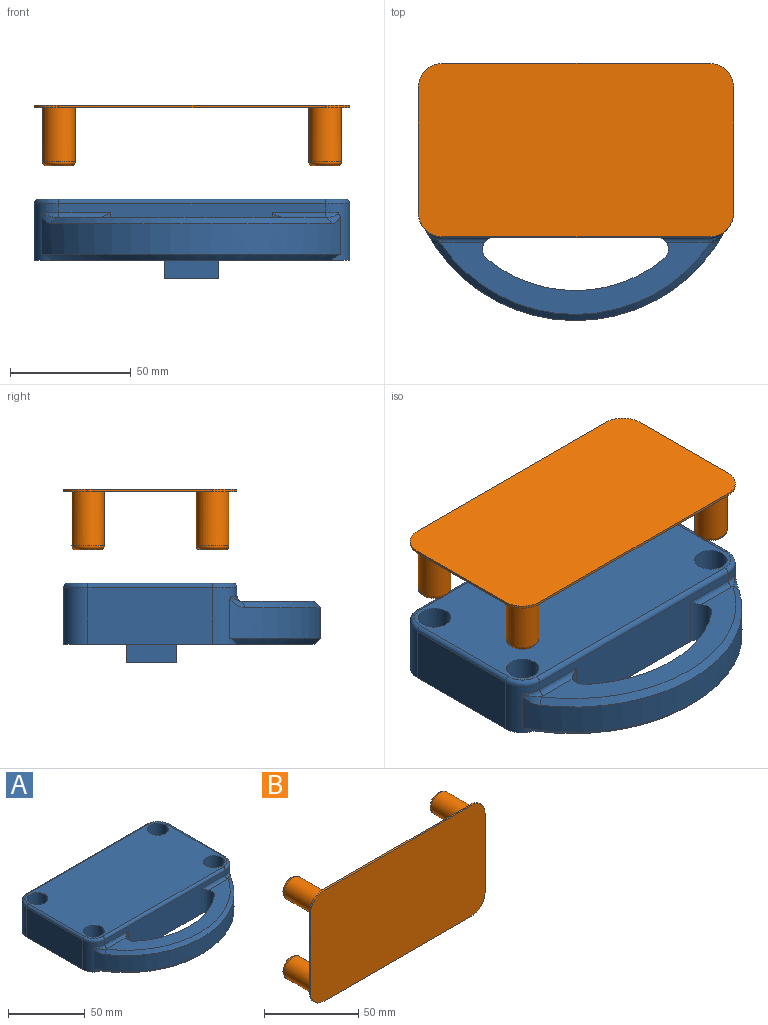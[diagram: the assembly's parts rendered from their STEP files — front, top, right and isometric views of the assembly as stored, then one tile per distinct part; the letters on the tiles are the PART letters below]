
ASSEMBLY  parts=2 mates=1
PART A: 40 faces, bbox 132.5x107.4x33 mm
  f0: plane 130.81x104.06mm, normal (0,0,-1), area 9557.4mm2, adj f1,f2,f3,f4,f5,f6,f7,f8
  f1: cylinder r=10.16mm len=23.5mm, axis (0,0,-1), area 222.8mm2, adj f0,f5,f6,f20,f23,f27,f33,f34
  f2: cylinder r=10.16mm len=23.5mm, axis (0,0,-1), area 375mm2, adj f0,f3,f12,f15
  f3: plane 110.49x23.5mm, normal (0,1,0), area 2596mm2, adj f0,f2,f4,f14
  f4: cylinder r=10.16mm len=23.5mm, axis (0,0,-1), area 375mm2, adj f0,f3,f5,f16
  f5: plane 51.64x23.5mm, normal (-1,0,0), area 1213.3mm2, adj f0,f1,f4,f18
  f6: plane 110.49x23.5mm, normal (0,-1,0), area 1729.2mm2, adj f0,f1,f7,f21,f25,f28,f29,f30
  f7: cylinder r=10.16mm len=23.5mm, axis (0,0,-1), area 247.5mm2, adj f0,f6,f12,f19,f23,f26,f31,f34
  f8: cylinder r=6.75mm len=25.4mm, axis (0,0,-1), area 1077.5mm2, adj f0,f13
  f9: cylinder r=6.75mm len=25.4mm, axis (0,0,-1), area 1077.5mm2, adj f0,f13
  f10: cylinder r=6.75mm len=25.4mm, axis (0,0,-1), area 1077.5mm2, adj f0,f13
  f11: cylinder r=6.75mm len=25.4mm, axis (0,0,-1), area 1077.5mm2, adj f0,f13
  f12: plane 51.64x23.5mm, normal (1,0,0), area 1213.3mm2, adj f0,f2,f7,f17
  f13: plane 127x68.15mm, normal (0,0,1), area 8023.7mm2, adj f8,f9,f10,f11,f14,f15,f16,f17
  f14: cylinder r=1.91mm len=110.49mm, axis (1,0,0), area 330.6mm2, adj f3,f13,f15,f16
  f15: torus R=8.26mm, axis (0,0,1), area 44.5mm2, adj f2,f13,f14,f17
  f16: torus R=8.26mm, axis (0,0,1), area 44.5mm2, adj f4,f13,f14,f18
  f17: cylinder r=1.91mm len=51.64mm, axis (0,-1,0), area 154.5mm2, adj f12,f13,f15,f19
  f18: cylinder r=1.91mm len=51.64mm, axis (0,1,0), area 154.5mm2, adj f5,f13,f16,f20
  f19: torus R=8.26mm, axis (0,0,1), area 44.5mm2, adj f7,f13,f17,f21
  f20: torus R=8.26mm, axis (0,0,1), area 44.5mm2, adj f1,f13,f18,f21
  f21: cylinder r=1.91mm len=110.49mm, axis (-1,0,0), area 330.6mm2, adj f6,f13,f19,f20
  f22: cylinder r=57.75mm len=73.49mm, axis (0,0,-1), area 1416.1mm2, adj f0,f24,f29,f30
  f23: cylinder r=70.2mm len=123.92mm, axis (0,0,-1), area 1951.8mm2, adj f1,f7,f31,f32,f33,f34
  f24: plane 112.4x30mm, normal (0,0,1), area 1180.6mm2, adj f22,f25,f26,f27,f28,f29,f30,f32
  f25: cylinder r=2.16mm len=21.98mm, axis (-1,0,0), area 67.5mm2, adj f6,f24,f26,f30
  f26: torus R=12.32mm, axis (0,0,-1), area 12.5mm2, adj f7,f24,f25,f31
  f27: torus R=12.32mm, axis (0,0,-1), area 15.1mm2, adj f1,f24,f28,f33
  f28: cylinder r=2.16mm len=21.49mm, axis (-1,0,0), area 65.8mm2, adj f6,f24,f27,f29
  f29: cylinder r=5.08mm len=19.94mm, axis (0,0,-1), area 226.7mm2, adj f0,f6,f22,f24,f28
  f30: cylinder r=5.08mm len=19.94mm, axis (0,0,-1), area 226.7mm2, adj f0,f6,f22,f24,f25
  f31: bspline ~6.22x5.83mm, area 18.5mm2, adj f7,f23,f26,f32
  f32: cone r=67.66mm half-angle=45deg, axis (0,0,-1), area 485.4mm2, adj f23,f24,f31,f33
  f33: bspline ~6.92x6.19mm, area 19.6mm2, adj f1,f23,f27,f32
  f34: cone r=70.2mm half-angle=45deg, axis (0,0,1), area 521.1mm2, adj f0,f1,f7,f23
  f35: plane 20.53x7.62mm, normal (-1,0,0), area 156.5mm2, adj f0,f36,f38,f39
  f36: plane 22.57x7.62mm, normal (0,1,0), area 172mm2, adj f0,f35,f37,f39
  f37: plane 20.53x7.62mm, normal (1,0,0), area 156.5mm2, adj f0,f36,f38,f39
  f38: plane 22.57x7.62mm, normal (0,-1,0), area 172mm2, adj f0,f35,f37,f39
  f39: plane 22.57x20.53mm, normal (0,0,-1), area 463.4mm2, adj f35,f36,f37,f38
PART B: 22 faces, bbox 130.8x25x72 mm
  f0: cylinder r=10.16mm len=10.16mm, axis (0,-1,0), area 16mm2, adj f1,f7,f8,f9
  f1: plane 110.49x1mm, normal (0,0,1), area 110.5mm2, adj f0,f2,f8,f9
  f2: cylinder r=10.16mm len=10.16mm, axis (0,-1,0), area 16mm2, adj f1,f3,f8,f9
  f3: plane 51.64x1mm, normal (-1,0,0), area 51.6mm2, adj f2,f4,f8,f9
  f4: cylinder r=10.16mm len=10.16mm, axis (0,-1,0), area 16mm2, adj f3,f5,f8,f9
  f5: plane 110.49x1mm, normal (0,0,-1), area 110.5mm2, adj f4,f6,f8,f9
  f6: cylinder r=10.16mm len=10.16mm, axis (0,-1,0), area 16mm2, adj f5,f7,f8,f9
  f7: plane 51.64x1mm, normal (1,0,0), area 51.6mm2, adj f0,f6,f8,f9
  f8: plane 130.81x71.96mm, normal (0,1,0), area 8751.6mm2, adj f0,f1,f2,f3,f4,f5,f6,f7
  f9: plane 130.81x71.96mm, normal (0,-1,0), area 9324.4mm2, adj f0,f1,f2,f3,f4,f5,f6,f7
  f10: cylinder r=6.75mm len=22.5mm, axis (0,-1,0), area 954.5mm2, adj f8,f18
  f11: plane 10.5x10.5mm, normal (0,1,0), area 86.6mm2, adj f18
  f12: cylinder r=6.75mm len=22.5mm, axis (0,-1,0), area 954.5mm2, adj f8,f20
  f13: plane 10.5x10.5mm, normal (0,1,0), area 86.6mm2, adj f20
  f14: cylinder r=6.75mm len=22.5mm, axis (0,-1,0), area 954.5mm2, adj f8,f21
  f15: plane 10.5x10.5mm, normal (0,1,0), area 86.6mm2, adj f21
  f16: cylinder r=6.75mm len=22.5mm, axis (0,-1,0), area 954.5mm2, adj f8,f19
  f17: plane 10.5x10.5mm, normal (0,1,0), area 86.6mm2, adj f19
  f18: torus R=5.25mm, axis (0,-1,0), area 91.9mm2, adj f10,f11
  f19: torus R=5.25mm, axis (0,-1,0), area 91.9mm2, adj f16,f17
  f20: torus R=5.25mm, axis (0,-1,0), area 91.9mm2, adj f12,f13
  f21: torus R=5.25mm, axis (0,-1,0), area 91.9mm2, adj f14,f15
PLACE A t=(-53.62,8.62,-0.12)mm fixed
PLACE B rot(axis=(-1,0,0),90deg) t=(-34.07,-5.25,51.45)mm
MATE slider B.f14 <-> A.f10  axis (0,0,-1) through (1.87,34.86,26.45)mm
